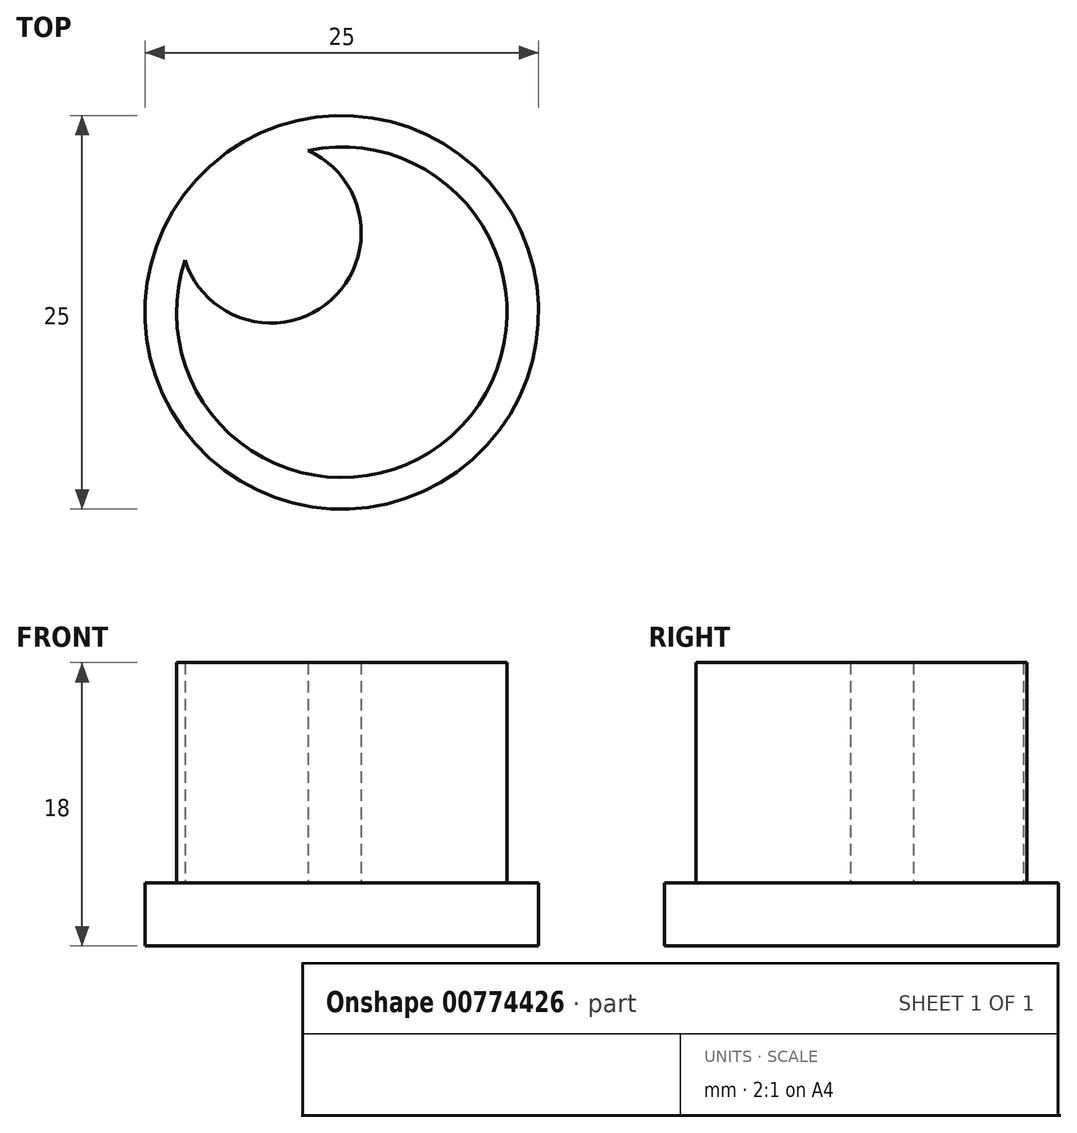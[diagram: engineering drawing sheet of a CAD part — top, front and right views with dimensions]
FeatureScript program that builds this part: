
annotation { "Feature Type Name" : "Feature", "Feature Type Description" : "" }
export const myFeature = defineFeature(function(context is Context, id is Id, definition is map)
    precondition{}
    {
        {
            var Q0;
            Q0=qCreatedBy(makeId("Top.planeOp"),FACE);
            var sketch = newSketch(context, id + "F0", { "sketchPlane" : qUnion([Q0])});
            skCircle(sketch, "E0", {"center": v(0, 0) * mm, "radius": 12.5 * mm});
            skSolve(sketch);
        }
        {
            var Q0;
            Q0=makeQuery(id+"F0.imprint","IMPRINT",FACE,{"disambiguationData":[TD([[makeQuery(id+"F0.imprint","IMPRINT",EDGE,{"derivedFrom":sQuery(id+"F0.wireOp",EDGE,"E0")}),1.0]])]});
            extrude(context, id + "F1", {"entities" : qUnion([Q0]), "depth" : 4 * mm, "offsetDistance" : 25 * mm});
        }
        {
            var Q0;
            Q0=makeQuery(id+"F1.opExtrude","CAP_FACE",FACE,{"disambiguationData":[OSD([sQuery(id+"F0.wireOp",EDGE,"E0")])],"isStart":false});
            var sketch = newSketch(context, id + "F2", { "sketchPlane" : qUnion([Q0])});
            skCircle(sketch, "E1", {"center": v(0, 0) * mm, "radius": 10.5 * mm});
            skSolve(sketch);
        }
        {
            var Q0;
            Q0=makeQuery(id+"F2.imprint","IMPRINT",FACE,{"disambiguationData":[TD([[makeQuery(id+"F2.imprint","IMPRINT",EDGE,{"derivedFrom":sQuery(id+"F2.wireOp",EDGE,"E1")}),1.0]])]});
            extrude(context, id + "F3", {"entities" : qUnion([Q0]), "operationType" : NewBodyOperationType.ADD, "depth" : 14 * mm, "offsetDistance" : 25 * mm});
        }
        {
            var Q0;
            Q0=makeQuery(id+"F1.opExtrude","CAP_FACE",FACE,{"disambiguationData":[OSD([sQuery(id+"F0.wireOp",EDGE,"E0")])],"isStart":false});
            var sketch = newSketch(context, id + "F4", { "sketchPlane" : qUnion([Q0])});
            skCircle(sketch, "E2", {"center": v(-4.5, 5.05) * mm, "radius": 5.73 * mm});
            skPoint(sketch, "E2.first.point", {"position": v(-8.28, 9.37) * mm});
            skPoint(sketch, "E2.second.point", {"position": v(0, 1.5) * mm});
            skPoint(sketch, "E2.third.point", {"position": v(-7.21, 0) * mm});
            skSolve(sketch);
        }
        {
            var Q0;
            Q0 = qSketchRegion(id + "F4", true);
            var Q1;
            Q1=sQuery(id+"F4.wireOp",EDGE,"E2");
            extrude(context, id + "F5", {"entities" : qUnion([Q0]), "operationType" : NewBodyOperationType.REMOVE, "surfaceEntities" : qUnion([Q1]), "depth" : 14 * mm, "offsetDistance" : 25 * mm});
        }
    });
